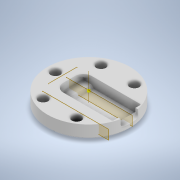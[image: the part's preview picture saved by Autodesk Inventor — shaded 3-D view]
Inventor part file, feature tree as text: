
AUTODESK INVENTOR PART (.ipt)
format: ipt  version: 2021 (Build 250183000, 183)  size: 694,784 bytes
history: native  units: in
note: dims shown in document units (in); Inventor stores cm internally (conversion verified against a paired STEP export)
features: sketch x10, extrude x8, fillet x4, chamfer x3, plane x3, mirror x2, other x1, pattern_circular x1
ambient origin geometry x8: Origin, YZ Plane, XZ Plane, XY Plane, X Axis, Y Axis, Z Axis, Center Point
bodies: Solid1 (feature_tree)
feature tree (32):
  extrude  "Extrusion1"  Depth=0.315in TaperAngle=0.0deg
  chamfer  "Chamfer2"  Distance=0.189in
  extrude  "Extrusion2"  Depth=0.1417in
  extrude  "Extrusion3"  Depth=0.2205in
  other  "Work Axis1"
  plane  "Work Plane1"
  extrude  "Extrusion5"  Depth=0.8268in
  extrude  "Extrusion4"  Depth=0.1969in
  fillet  "Fillet4"  Radius=0.063in
  pattern_circular  "Circular Pattern2"  [2 undecoded]
  fillet  "Fillet7"  [1 undecoded]
  extrude  "Initals"  Depth=0.0394in
  fillet  "Fillet9"  Radius=0.1181in
  fillet  "Fillet10"  Radius=0.0315in
  mirror  "Mirror6"
  sketch  "Sketch18"  dims[d18=0.2047in d19=0.0in d23=0.8268in]
  chamfer  "Chamfer4"  Distance=1.1811in
  chamfer  "Chamfer5"  Distance=0.5906in
  plane  "Work Plane5"
  extrude  "Extrusion13"  Depth=0.9728in
  mirror  "Mirror7"
  plane  "Work Plane6"
  extrude  "Extrusion14"  Depth=0.4864in
  sketch  "Sketch1"  dims[d0=2.0472in d3=0.315in d4=0.0in]
  sketch  "Sketch2"  dims[d5=1.4315in]
  sketch  "Sketch3"  dims[d6=0.7079in]
  sketch  "Sketch4"  dims[d7=0.3539in]
  sketch  "Sketch7"  dims[d8=0.4882in d9=0.189in d10=0.0in]
  sketch  "Sketch12"  dims[d11=0.0in d14=0.1417in]
  sketch  "Sketch13"  dims[d15=0.0in d16=0.0in d17=0.2205in]
  sketch  "Sketch19"  dims[d24=0.3539in d31=0.1969in d32=0.063in d33=0.0in]
  sketch  "Sketch20"  dims[d44=0.1417in d47=0.0in d48=0.0in d49=0.0in d51=0.0in d54=0.0394in d55=0.0in d56=45.0deg d58=0.0394in d59=0.1181in d60=1.9685in d61=240.0deg d72=0.0315in d80=1.1811in d81=0.5906in d82=0.9728in d83=0.4864in d84=0.0394in d85=0.0in d86=0.547in d87=0.2735in d88=0.0787in d89=0.0in d90=0.0787in d98=0.1024in d99=0.0in d100=0.0in d101=0.2362in d102=0.0315in d103=0.0315in d104=0.2953in d105=0.1575in d106=0.1969in d107=0.063in d108=0.0787in d109=45.0deg d110=0.063in d111=0.0787in d112=45.0deg d114=0.5906in d115=0.0in d116=0.0in d117=-0.1575in d118=0.3937in d119=0.0in d91=0.0197in d92=0.0344in d93=0.0197in d94=0.0344in]
note: 3 required parameter values undecoded (feature->parameter linkage not recoverable at this tier; creation-order binding heuristic only, values carry confidence <= 0.55)
